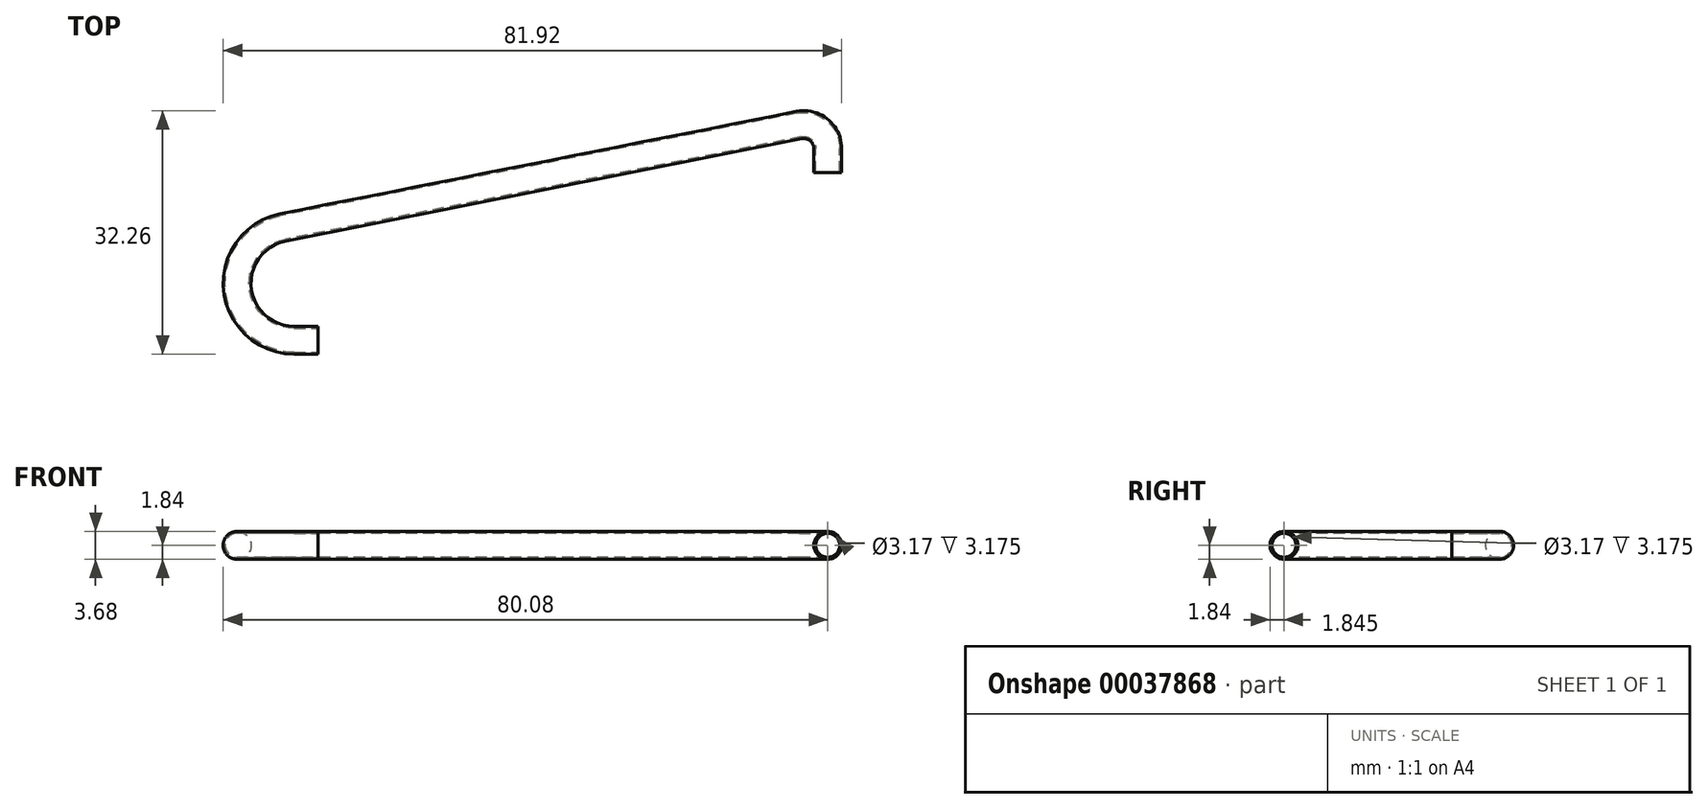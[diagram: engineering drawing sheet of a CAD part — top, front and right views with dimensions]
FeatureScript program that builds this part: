
annotation { "Feature Type Name" : "Feature", "Feature Type Description" : "" }
export const myFeature = defineFeature(function(context is Context, id is Id, definition is map)
    precondition{}
    {
        {
            var Q0;
            Q0=qCreatedBy(makeId("Top.planeOp"),FACE);
            var sketch = newSketch(context, id + "F0", { "sketchPlane" : qUnion([Q0])});
            skLineSegment(sketch, "E0.right", {"start": v(0, -19.05) * mm, "end": v(0, 0) * mm, "construction": true});
            skLineSegment(sketch, "E1", {"start": v(-3.8, 6.29) * mm, "end": v(-72.16, -7.27) * mm});
            skLineSegment(sketch, "E0.bottom", {"start": v(0, -19.05) * mm, "end": v(-15.92, -19.05) * mm, "construction": true});
            skArc(sketch, "E2", {"start": v(-72.16, -7.27) * mm, "mid": v(-78.2, -15.41) * mm, "end": v(-70.7, -22.22) * mm});
            skLineSegment(sketch, "E3", {"start": v(-67.52, -9.53) * mm, "end": v(-15.92, -9.52) * mm, "construction": true});
            skLineSegment(sketch, "E4", {"start": v(-15.92, -22.22) * mm, "end": v(-67.52, -22.22) * mm, "construction": true});
            skLineSegment(sketch, "E5", {"start": v(-15.92, -9.52) * mm, "end": v(-15.92, -19.05) * mm, "construction": true});
            skLineSegment(sketch, "E6", {"start": v(-67.52, -22.22) * mm, "end": v(-70.7, -22.22) * mm});
            skLineSegment(sketch, "E7", {"start": v(0, 0) * mm, "end": v(0, 3.18) * mm});
            skArc(sketch, "E8", {"start": v(0, 3.18) * mm, "mid": v(-1.16, 5.63) * mm, "end": v(-3.8, 6.29) * mm});
            skLineSegment(sketch, "E9", {"start": v(-15.92, -19.05) * mm, "end": v(-15.92, -22.22) * mm, "construction": true});
            skLineSegment(sketch, "E10", {"start": v(-67.52, -9.53) * mm, "end": v(-67.52, -6.35) * mm});
            skSolve(sketch);
        }
        {
            var Q0;
            Q0=qCreatedBy(makeId("Front.planeOp"),FACE);
            var sketch = newSketch(context, id + "F1", { "sketchPlane" : qUnion([Q0])});
            skLineSegment(sketch, "E11.rect.bottom", {"start": v(1.84, -1.84) * mm, "end": v(-1.84, -1.84) * mm});
            skLineSegment(sketch, "E11.rect.top", {"start": v(1.84, 1.84) * mm, "end": v(-1.84, 1.84) * mm});
            skLineSegment(sketch, "E11.rect.left", {"start": v(1.84, -1.84) * mm, "end": v(1.84, 1.84) * mm});
            skLineSegment(sketch, "E11.rect.right", {"start": v(-1.84, -1.84) * mm, "end": v(-1.84, 1.84) * mm});
            skPoint(sketch, "E11.rect.middle", {"position": v(0, 0) * mm});
            skCircle(sketch, "E12", {"center": v(0, 0) * mm, "radius": 1.59 * mm});
            skSolve(sketch);
        }
        {
            var Q0;
            Q0 = qSketchRegion(id + "F1", true);
            var Q1;
            Q1=sQuery(id+"F0.wireOp",EDGE,"E7");
            var Q2;
            Q2=sQuery(id+"F0.wireOp",EDGE,"E8");
            var Q3;
            Q3=sQuery(id+"F0.wireOp",EDGE,"E1");
            var Q4;
            Q4=sQuery(id+"F0.wireOp",EDGE,"E2");
            var Q5;
            Q5=sQuery(id+"F0.wireOp",EDGE,"E6");
            sweep(context, id + "F2", {"profiles" : qUnion([Q0]), "path" : qUnion([Q1, Q2, Q3, Q4, Q5])});
        }
        {
            var Q0;
            Q0=makeQuery(id+"F2.opSweep","SWEPT_EDGE",EDGE,{"disambiguationData":[OSD([sQuery(id+"F0.wireOp",EDGE,"E1"),sQuery(id+"F1.wireOp",EDGE,"E11.rect.top"),sQuery(id+"F1.wireOp",EDGE,"E11.rect.right")])]});
            var Q1;
            Q1=makeQuery(id+"F2.opSweep","SWEPT_EDGE",EDGE,{"disambiguationData":[OSD([sQuery(id+"F0.wireOp",EDGE,"E1"),sQuery(id+"F1.wireOp",EDGE,"E11.rect.bottom"),sQuery(id+"F1.wireOp",EDGE,"E11.rect.right")])]});
            var Q2;
            Q2=makeQuery(id+"F2.opSweep","SWEPT_EDGE",EDGE,{"disambiguationData":[OSD([sQuery(id+"F0.wireOp",EDGE,"E1"),sQuery(id+"F1.wireOp",EDGE,"E11.rect.top"),sQuery(id+"F1.wireOp",EDGE,"E11.rect.left")])]});
            var Q3;
            Q3=makeQuery(id+"F2.opSweep","SWEPT_EDGE",EDGE,{"disambiguationData":[OSD([sQuery(id+"F0.wireOp",EDGE,"E1"),sQuery(id+"F1.wireOp",EDGE,"E11.rect.bottom"),sQuery(id+"F1.wireOp",EDGE,"E11.rect.left")])]});
            fillet(context, id + "F3", {"entities" : qUnion([Q0, Q1, Q2, Q3]), "radius" : 1.84 * mm, "tangentPropagation" : true, "allowEdgeOverflow" : false});
        }
    });
